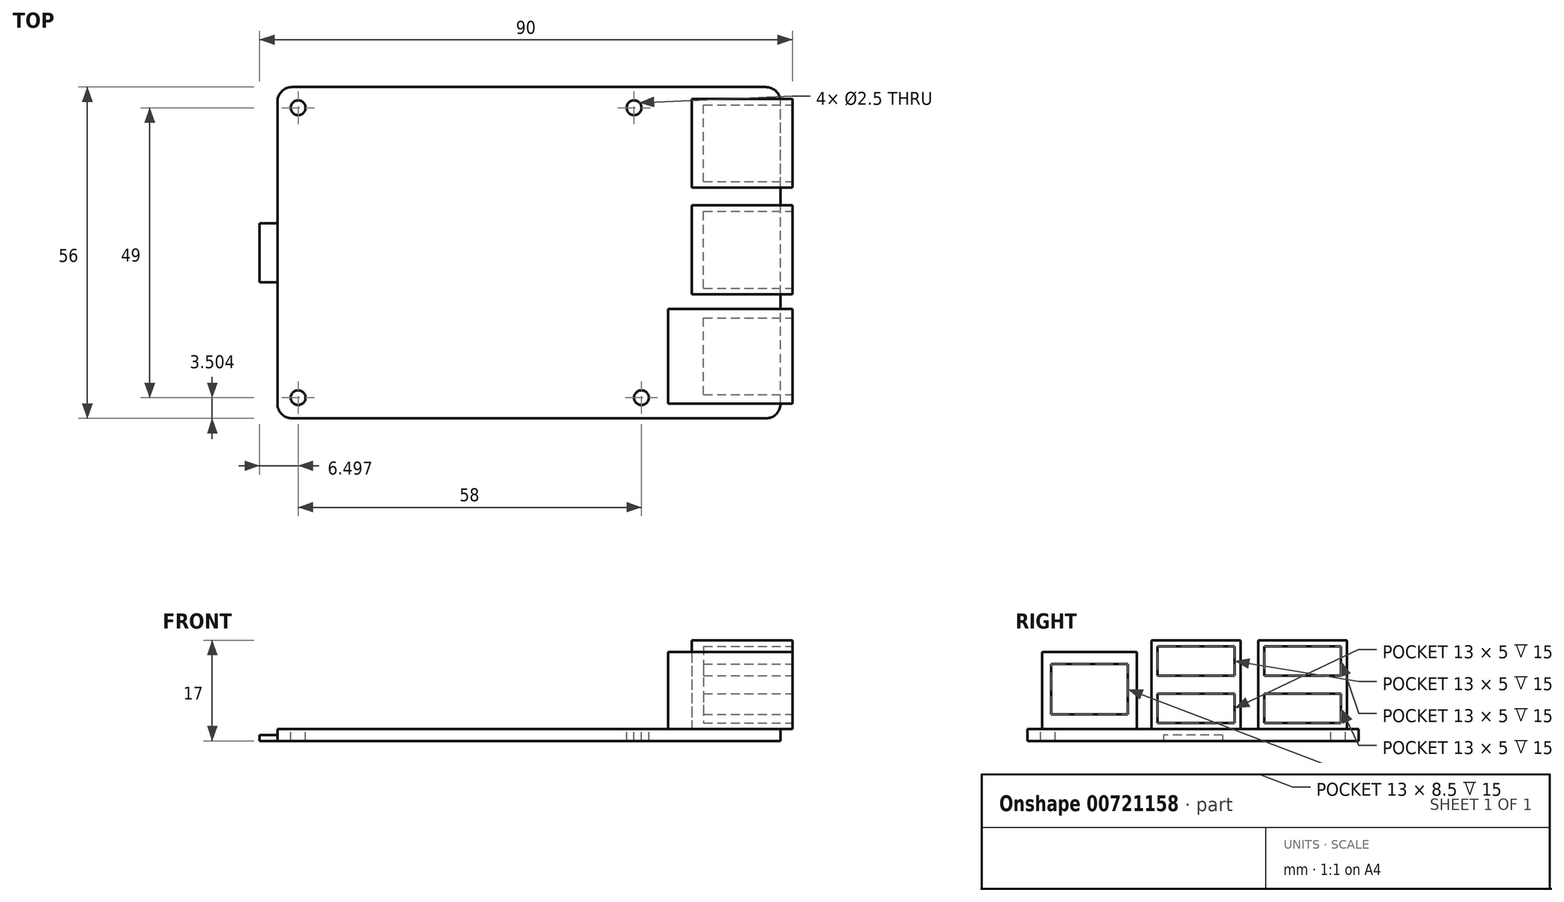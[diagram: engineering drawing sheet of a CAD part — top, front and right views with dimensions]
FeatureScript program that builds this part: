
annotation { "Feature Type Name" : "Feature", "Feature Type Description" : "" }
export const myFeature = defineFeature(function(context is Context, id is Id, definition is map)
    precondition{}
    {
        {
            var Q0;
            Q0=qCreatedBy(makeId("Top.planeOp"),FACE);
            var sketch = newSketch(context, id + "F0", { "sketchPlane" : qUnion([Q0])});
            skLineSegment(sketch, "E0.bottom", {"start": v(-2.05, 10.56) * mm, "end": v(82.95, 10.56) * mm});
            skLineSegment(sketch, "E0.top", {"start": v(-2.05, 66.56) * mm, "end": v(82.95, 66.56) * mm});
            skLineSegment(sketch, "E0.left", {"start": v(-2.05, 10.56) * mm, "end": v(-2.05, 66.56) * mm});
            skLineSegment(sketch, "E0.right", {"start": v(82.95, 10.56) * mm, "end": v(82.95, 66.56) * mm});
            skSolve(sketch);
        }
        {
            var Q0;
            Q0 = qSketchRegion(id + "F0", true);
            extrude(context, id + "F1", {"entities" : qUnion([Q0]), "depth" : 2 * mm, "offsetDistance" : 25 * mm});
        }
        {
            var Q0;
            Q0=makeQuery(id+"F1.opExtrude","CAP_FACE",FACE,{"disambiguationData":[OSD([sQuery(id+"F0.wireOp",EDGE,"E0.bottom"),sQuery(id+"F0.wireOp",EDGE,"E0.top"),sQuery(id+"F0.wireOp",EDGE,"E0.left"),sQuery(id+"F0.wireOp",EDGE,"E0.right")])],"isStart":false});
            var sketch = newSketch(context, id + "F2", { "sketchPlane" : qUnion([Q0])});
            skCircle(sketch, "E1", {"center": v(1.45, 63.06) * mm, "radius": 1.25 * mm});
            skCircle(sketch, "E2", {"center": v(1.45, 14.06) * mm, "radius": 1.25 * mm});
            skCircle(sketch, "E3", {"center": v(58.2, 63.06) * mm, "radius": 1.25 * mm});
            skCircle(sketch, "E4", {"center": v(59.45, 14.06) * mm, "radius": 1.25 * mm});
            skSolve(sketch);
        }
        {
            var Q0;
            Q0 = qSketchRegion(id + "F2", true);
            extrude(context, id + "F3", {"entities" : qUnion([Q0]), "operationType" : NewBodyOperationType.REMOVE, "endBound" : BoundingType.UP_TO_NEXT, "oppositeDirection" : true, "depth" : 25 * mm, "offsetDistance" : 25 * mm});
        }
        {
            var Q0;
            Q0=makeQuery(id+"F1.opExtrude","SWEPT_EDGE",EDGE,{"disambiguationData":[OSD([sQuery(id+"F0.wireOp",EDGE,"E0.bottom"),sQuery(id+"F0.wireOp",EDGE,"E0.right")])]});
            var Q1;
            Q1=makeQuery(id+"F1.opExtrude","SWEPT_EDGE",EDGE,{"disambiguationData":[OSD([sQuery(id+"F0.wireOp",EDGE,"E0.top"),sQuery(id+"F0.wireOp",EDGE,"E0.right")])]});
            var Q2;
            Q2=makeQuery(id+"F1.opExtrude","SWEPT_EDGE",EDGE,{"disambiguationData":[OSD([sQuery(id+"F0.wireOp",EDGE,"E0.bottom"),sQuery(id+"F0.wireOp",EDGE,"E0.left")])]});
            var Q3;
            Q3=makeQuery(id+"F1.opExtrude","SWEPT_EDGE",EDGE,{"disambiguationData":[OSD([sQuery(id+"F0.wireOp",EDGE,"E0.top"),sQuery(id+"F0.wireOp",EDGE,"E0.left")])]});
            fillet(context, id + "F4", {"entities" : qUnion([Q0, Q1, Q2, Q3]), "radius" : 2.5 * mm, "tangentPropagation" : true, "allowEdgeOverflow" : false});
        }
        {
            var Q0;
            Q0=makeQuery(id+"F1.opExtrude","CAP_FACE",FACE,{"disambiguationData":[OSD([sQuery(id+"F0.wireOp",EDGE,"E0.bottom"),sQuery(id+"F0.wireOp",EDGE,"E0.top"),sQuery(id+"F0.wireOp",EDGE,"E0.left"),sQuery(id+"F0.wireOp",EDGE,"E0.right")])],"isStart":false});
            var sketch = newSketch(context, id + "F5", { "sketchPlane" : qUnion([Q0])});
            skLineSegment(sketch, "E5.bottom", {"start": v(67.95, 64.56) * mm, "end": v(84.95, 64.56) * mm});
            skLineSegment(sketch, "E5.top", {"start": v(67.95, 49.56) * mm, "end": v(84.95, 49.56) * mm});
            skLineSegment(sketch, "E5.left", {"start": v(67.95, 64.56) * mm, "end": v(67.95, 49.56) * mm});
            skLineSegment(sketch, "E5.right", {"start": v(84.95, 64.56) * mm, "end": v(84.95, 49.56) * mm});
            skLineSegment(sketch, "E6.bottom", {"start": v(67.95, 46.56) * mm, "end": v(84.95, 46.56) * mm});
            skLineSegment(sketch, "E6.top", {"start": v(67.95, 31.56) * mm, "end": v(84.95, 31.56) * mm});
            skLineSegment(sketch, "E6.left", {"start": v(67.95, 46.56) * mm, "end": v(67.95, 31.56) * mm});
            skLineSegment(sketch, "E6.right", {"start": v(84.95, 46.56) * mm, "end": v(84.95, 31.56) * mm});
            skSolve(sketch);
        }
        {
            var Q0;
            Q0 = qSketchRegion(id + "F5", true);
            extrude(context, id + "F6", {"entities" : qUnion([Q0]), "operationType" : NewBodyOperationType.ADD, "depth" : 15 * mm, "offsetDistance" : 25 * mm});
        }
        {
            var Q0;
            Q0=makeQuery(id+"F6.opExtrude","SWEPT_FACE",FACE,{"disambiguationData":[OSD([sQuery(id+"F5.wireOp",EDGE,"E6.right")])]});
            var sketch = newSketch(context, id + "F7", { "sketchPlane" : qUnion([Q0])});
            skLineSegment(sketch, "E7.bottom", {"start": v(32.56, 16) * mm, "end": v(45.56, 16) * mm});
            skLineSegment(sketch, "E7.top", {"start": v(32.56, 11) * mm, "end": v(45.56, 11) * mm});
            skLineSegment(sketch, "E7.left", {"start": v(32.56, 16) * mm, "end": v(32.56, 11) * mm});
            skLineSegment(sketch, "E7.right", {"start": v(45.56, 16) * mm, "end": v(45.56, 11) * mm});
            skLineSegment(sketch, "E8.bottom", {"start": v(32.56, 8) * mm, "end": v(45.56, 8) * mm});
            skLineSegment(sketch, "E8.top", {"start": v(32.56, 3) * mm, "end": v(45.56, 3) * mm});
            skLineSegment(sketch, "E8.left", {"start": v(32.56, 8) * mm, "end": v(32.56, 3) * mm});
            skLineSegment(sketch, "E8.right", {"start": v(45.56, 8) * mm, "end": v(45.56, 3) * mm});
            skLineSegment(sketch, "E9.bottom", {"start": v(50.56, 16) * mm, "end": v(63.56, 16) * mm});
            skLineSegment(sketch, "E9.top", {"start": v(50.56, 11) * mm, "end": v(63.56, 11) * mm});
            skLineSegment(sketch, "E9.left", {"start": v(50.56, 16) * mm, "end": v(50.56, 11) * mm});
            skLineSegment(sketch, "E9.right", {"start": v(63.56, 16) * mm, "end": v(63.56, 11) * mm});
            skLineSegment(sketch, "E10.bottom", {"start": v(50.56, 8) * mm, "end": v(63.56, 8) * mm});
            skLineSegment(sketch, "E10.top", {"start": v(50.56, 3) * mm, "end": v(63.56, 3) * mm});
            skLineSegment(sketch, "E10.left", {"start": v(50.56, 8) * mm, "end": v(50.56, 3) * mm});
            skLineSegment(sketch, "E10.right", {"start": v(63.56, 8) * mm, "end": v(63.56, 3) * mm});
            skSolve(sketch);
        }
        {
            var Q0;
            Q0 = qSketchRegion(id + "F7", true);
            extrude(context, id + "F8", {"entities" : qUnion([Q0]), "operationType" : NewBodyOperationType.REMOVE, "oppositeDirection" : true, "depth" : 15 * mm, "offsetDistance" : 25 * mm});
        }
        {
            var Q0;
            Q0=makeQuery(id+"F1.opExtrude","CAP_FACE",FACE,{"disambiguationData":[OSD([sQuery(id+"F0.wireOp",EDGE,"E0.bottom"),sQuery(id+"F0.wireOp",EDGE,"E0.top"),sQuery(id+"F0.wireOp",EDGE,"E0.left"),sQuery(id+"F0.wireOp",EDGE,"E0.right")])],"isStart":false});
            var sketch = newSketch(context, id + "F9", { "sketchPlane" : qUnion([Q0])});
            skLineSegment(sketch, "E11.bottom", {"start": v(63.95, 29.06) * mm, "end": v(84.95, 29.06) * mm});
            skLineSegment(sketch, "E11.top", {"start": v(63.95, 13.06) * mm, "end": v(84.95, 13.06) * mm});
            skLineSegment(sketch, "E11.left", {"start": v(63.95, 29.06) * mm, "end": v(63.95, 13.06) * mm});
            skLineSegment(sketch, "E11.right", {"start": v(84.95, 29.06) * mm, "end": v(84.95, 13.06) * mm});
            skSolve(sketch);
        }
        {
            var Q0;
            Q0 = qSketchRegion(id + "F9", true);
            extrude(context, id + "F10", {"entities" : qUnion([Q0]), "operationType" : NewBodyOperationType.ADD, "depth" : 13 * mm, "offsetDistance" : 25 * mm});
        }
        {
            var Q0;
            Q0=makeQuery(id+"F10.opExtrude","SWEPT_FACE",FACE,{"disambiguationData":[OSD([sQuery(id+"F9.wireOp",EDGE,"E11.right")])]});
            var sketch = newSketch(context, id + "F11", { "sketchPlane" : qUnion([Q0])});
            skLineSegment(sketch, "E12.bottom", {"start": v(14.56, 13) * mm, "end": v(27.56, 13) * mm});
            skLineSegment(sketch, "E12.top", {"start": v(14.56, 4.5) * mm, "end": v(27.56, 4.5) * mm});
            skLineSegment(sketch, "E12.left", {"start": v(14.56, 13) * mm, "end": v(14.56, 4.5) * mm});
            skLineSegment(sketch, "E12.right", {"start": v(27.56, 13) * mm, "end": v(27.56, 4.5) * mm});
            skSolve(sketch);
        }
        {
            var Q0;
            Q0 = qSketchRegion(id + "F11", true);
            extrude(context, id + "F12", {"entities" : qUnion([Q0]), "operationType" : NewBodyOperationType.REMOVE, "oppositeDirection" : true, "depth" : 15 * mm, "offsetDistance" : 25 * mm});
        }
        {
            var Q0;
            Q0=makeQuery(id+"F1.opExtrude","SWEPT_FACE",FACE,{"disambiguationData":[OSD([sQuery(id+"F0.wireOp",EDGE,"E0.left")])]});
            var sketch = newSketch(context, id + "F13", { "sketchPlane" : qUnion([Q0])});
            skLineSegment(sketch, "E13.bottom", {"start": v(-43.56, 1) * mm, "end": v(-33.56, 1) * mm});
            skLineSegment(sketch, "E13.top", {"start": v(-43.56, 0) * mm, "end": v(-33.56, 0) * mm});
            skLineSegment(sketch, "E13.left", {"start": v(-43.56, 1) * mm, "end": v(-43.56, 0) * mm});
            skLineSegment(sketch, "E13.right", {"start": v(-33.56, 1) * mm, "end": v(-33.56, 0) * mm});
            skLineSegment(sketch, "E14", {"start": v(-64.06, 0) * mm, "end": v(-43.56, 0) * mm, "construction": true});
            skLineSegment(sketch, "E15", {"start": v(-13.06, 0) * mm, "end": v(-33.56, 0) * mm, "construction": true});
            skSolve(sketch);
        }
        {
            var Q0;
            Q0 = qSketchRegion(id + "F13", true);
            extrude(context, id + "F14", {"entities" : qUnion([Q0]), "operationType" : NewBodyOperationType.ADD, "depth" : 3 * mm, "offsetDistance" : 25 * mm});
        }
    });
